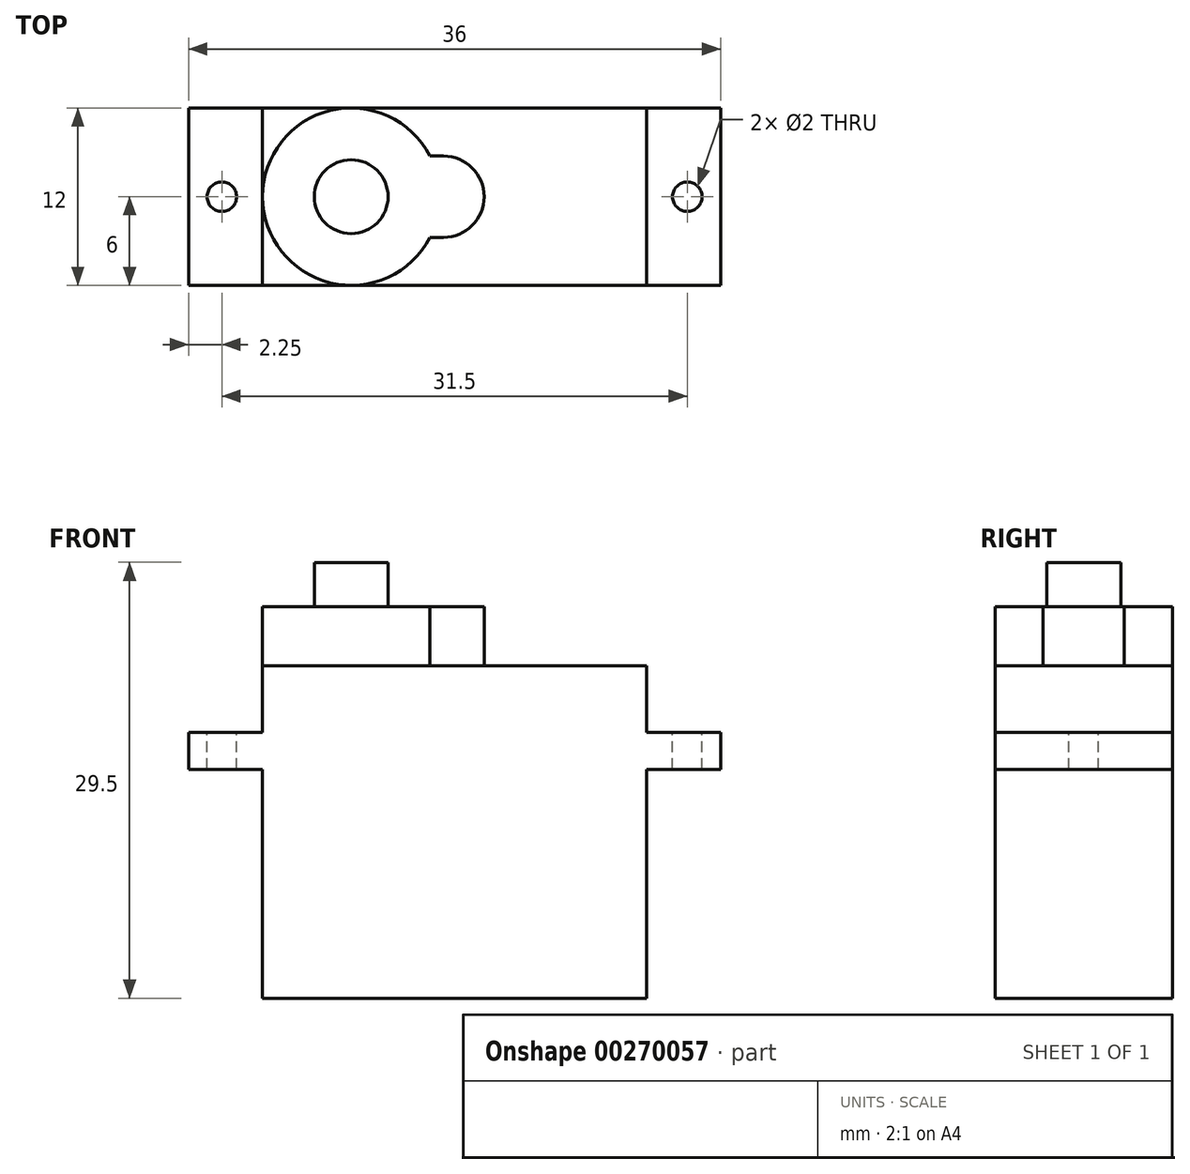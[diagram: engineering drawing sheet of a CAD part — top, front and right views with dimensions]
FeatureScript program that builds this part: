
annotation { "Feature Type Name" : "Feature", "Feature Type Description" : "" }
export const myFeature = defineFeature(function(context is Context, id is Id, definition is map)
    precondition{}
    {
        {
            var Q0;
            Q0=qCreatedBy(makeId("Front.planeOp"),FACE);
            var sketch = newSketch(context, id + "F0", { "sketchPlane" : qUnion([Q0])});
            skLineSegment(sketch, "E0.bottom", {"start": v(-13, 17.93) * mm, "end": v(13, 17.93) * mm});
            skLineSegment(sketch, "E0.top", {"start": v(-13, -4.57) * mm, "end": v(13, -4.57) * mm});
            skLineSegment(sketch, "E0.left", {"start": v(-13, 17.93) * mm, "end": v(-13, 13.43) * mm});
            skLineSegment(sketch, "E0.right", {"start": v(13, 17.93) * mm, "end": v(13, 13.43) * mm});
            skLineSegment(sketch, "E1.bottom", {"start": v(-13, 13.43) * mm, "end": v(-18, 13.43) * mm});
            skLineSegment(sketch, "E1.top", {"start": v(-13, 10.93) * mm, "end": v(-18, 10.93) * mm});
            skLineSegment(sketch, "E1.right", {"start": v(-18, 13.43) * mm, "end": v(-18, 10.93) * mm});
            skLineSegment(sketch, "E2.bottom", {"start": v(13, 13.43) * mm, "end": v(18, 13.43) * mm});
            skLineSegment(sketch, "E2.top", {"start": v(13, 10.93) * mm, "end": v(18, 10.93) * mm});
            skLineSegment(sketch, "E2.right", {"start": v(18, 13.43) * mm, "end": v(18, 10.93) * mm});
            skLineSegment(sketch, "E3.trimOffspring", {"start": v(-13, 10.93) * mm, "end": v(-13, -4.57) * mm});
            skLineSegment(sketch, "E4.trimOffspring", {"start": v(13, 10.93) * mm, "end": v(13, -4.57) * mm});
            skSolve(sketch);
        }
        {
            var Q0;
            Q0=makeQuery(id+"F0.imprint","IMPRINT",FACE,{"disambiguationData":[TD([[makeQuery(id+"F0.imprint","IMPRINT",EDGE,{"derivedFrom":sQuery(id+"F0.wireOp",EDGE,"E0.bottom")}),-1.0]])]});
            extrude(context, id + "F1", {"entities" : qUnion([Q0]), "endBound" : BoundingType.SYMMETRIC, "depth" : 12 * mm});
        }
        {
            var Q0;
            Q0=makeQuery(id+"F1.opExtrude","SWEPT_FACE",FACE,{"disambiguationData":[OSD([sQuery(id+"F0.wireOp",EDGE,"E0.bottom")])]});
            var sketch = newSketch(context, id + "F2", { "sketchPlane" : qUnion([Q0])});
            skArc(sketch, "E5", {"start": v(-1.67, 2.75) * mm, "mid": v(-13, 0) * mm, "end": v(-1.67, -2.75) * mm});
            skPoint(sketch, "E5.centerSnap0", {"position": v(-13, 0) * mm});
            skArc(sketch, "E6", {"start": v(-0.75, -2.75) * mm, "mid": v(2, 0) * mm, "end": v(-0.75, 2.75) * mm});
            skLineSegment(sketch, "E7", {"start": v(-0.75, 2.75) * mm, "end": v(-1.67, 2.75) * mm});
            skLineSegment(sketch, "E8", {"start": v(-0.75, -2.75) * mm, "end": v(-1.67, -2.75) * mm});
            skSolve(sketch);
        }
        {
            var Q0;
            {var subQ0=sQuery(id+"F2.wireOp",EDGE,"E6");Q0=makeQuery(id+"F2.imprint","IMPRINT",FACE,{"disambiguationData":[TD([[makeQuery(id+"F2.imprint","IMPRINT",EDGE,{"derivedFrom":subQ0}),1.0]])]});}
            extrude(context, id + "F3", {"entities" : qUnion([Q0]), "operationType" : NewBodyOperationType.ADD, "depth" : 4 * mm});
        }
        {
            var Q0;
            Q0=makeQuery(id+"F1.opExtrude","SWEPT_FACE",FACE,{"disambiguationData":[OSD([sQuery(id+"F0.wireOp",EDGE,"E2.bottom")])]});
            var sketch = newSketch(context, id + "F4", { "sketchPlane" : qUnion([Q0])});
            skCircle(sketch, "E9", {"center": v(15.75, 0) * mm, "radius": 1 * mm});
            skPoint(sketch, "E9.centerSnap0", {"position": v(18, 0) * mm});
            skCircle(sketch, "E10", {"center": v(-15.75, 0) * mm, "radius": 1 * mm});
            skSolve(sketch);
        }
        {
            var Q0;
            Q0=makeQuery(id+"F4.imprint","IMPRINT",FACE,{"disambiguationData":[TD([[makeQuery(id+"F4.imprint","IMPRINT",EDGE,{"derivedFrom":sQuery(id+"F4.wireOp",EDGE,"E9")}),1.0]])]});
            var Q1;
            Q1=makeQuery(id+"F4.imprint","IMPRINT",FACE,{"disambiguationData":[TD([[makeQuery(id+"F4.imprint","IMPRINT",EDGE,{"derivedFrom":sQuery(id+"F4.wireOp",EDGE,"E10")}),1.0]])]});
            extrude(context, id + "F5", {"entities" : qUnion([Q0, Q1]), "operationType" : NewBodyOperationType.REMOVE, "endBound" : BoundingType.THROUGH_ALL, "oppositeDirection" : true, "depth" : 25 * mm});
        }
        {
            var Q0;
            Q0=makeQuery(id+"F3.opExtrude","CAP_FACE",FACE,{"disambiguationData":[OSD([sQuery(id+"F2.wireOp",EDGE,"E5"),sQuery(id+"F2.wireOp",EDGE,"E6")])],"isStart":false});
            var sketch = newSketch(context, id + "F6", { "sketchPlane" : qUnion([Q0])});
            skCircle(sketch, "E11", {"center": v(-7, 0) * mm, "radius": 2.5 * mm});
            skSolve(sketch);
        }
        {
            var Q0;
            Q0=makeQuery(id+"F6.imprint","IMPRINT",FACE,{"disambiguationData":[TD([[makeQuery(id+"F6.imprint","IMPRINT",EDGE,{"derivedFrom":sQuery(id+"F6.wireOp",EDGE,"E11")}),1.0]])]});
            extrude(context, id + "F7", {"entities" : qUnion([Q0]), "operationType" : NewBodyOperationType.ADD, "depth" : 3 * mm});
        }
    });
